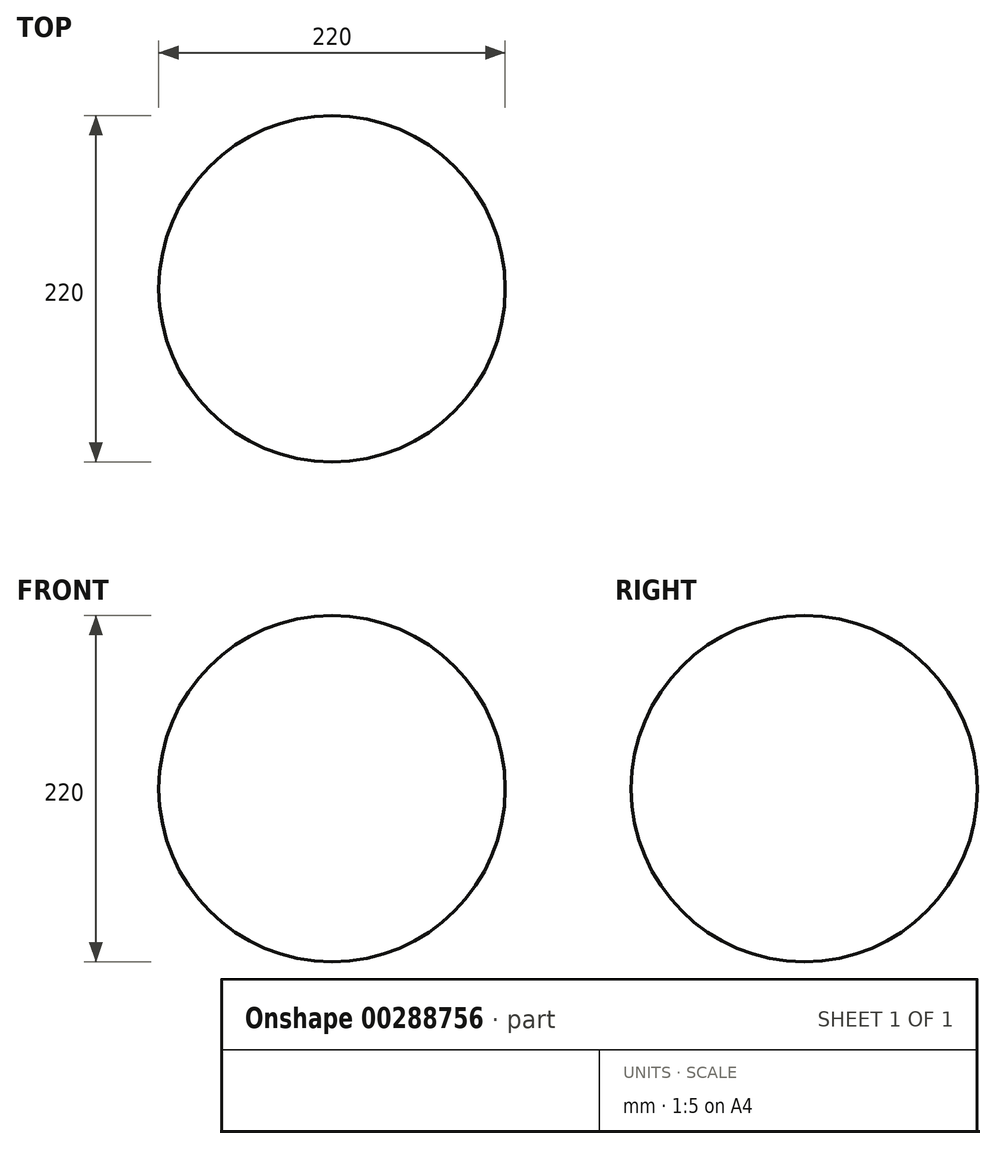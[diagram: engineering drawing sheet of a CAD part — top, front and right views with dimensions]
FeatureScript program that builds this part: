
annotation { "Feature Type Name" : "Feature", "Feature Type Description" : "" }
export const myFeature = defineFeature(function(context is Context, id is Id, definition is map)
    precondition{}
    {
        {
            var Q0;
            Q0=qCreatedBy(makeId("Top.planeOp"),FACE);
            var sketch = newSketch(context, id + "F0", { "sketchPlane" : qUnion([Q0])});
            skArc(sketch, "E0", {"start": v(-110, 0) * mm, "mid": v(0, -110) * mm, "end": v(110, 0) * mm});
            skLineSegment(sketch, "E1", {"start": v(-110, 0) * mm, "end": v(110, 0) * mm});
            skSolve(sketch);
        }
        {
            var Q0;
            Q0=makeQuery(id+"F0.imprint","IMPRINT",FACE,{"disambiguationData":[TD([[makeQuery(id+"F0.imprint","IMPRINT",EDGE,{"derivedFrom":sQuery(id+"F0.wireOp",EDGE,"9as072aN-jNIo-leGN-kAtz-eR7s1DJ2pvbN")}),1.0]])]});
            var Q1;
            Q1=sQuery(id+"F0.wireOp",EDGE,"E0");
            var Q2;
            Q2=sQuery(id+"F0.wireOp",EDGE,"E1");
            revolve(context, id + "F1", {"bodyType" : ToolBodyType.SURFACE, "entities" : qUnion([Q0]), "surfaceEntities" : qUnion([Q1]), "axis" : qUnion([Q2]), "revolveType" : RevolveType.ONE_DIRECTION, "angle" : 360 * degree});
        }
    });
